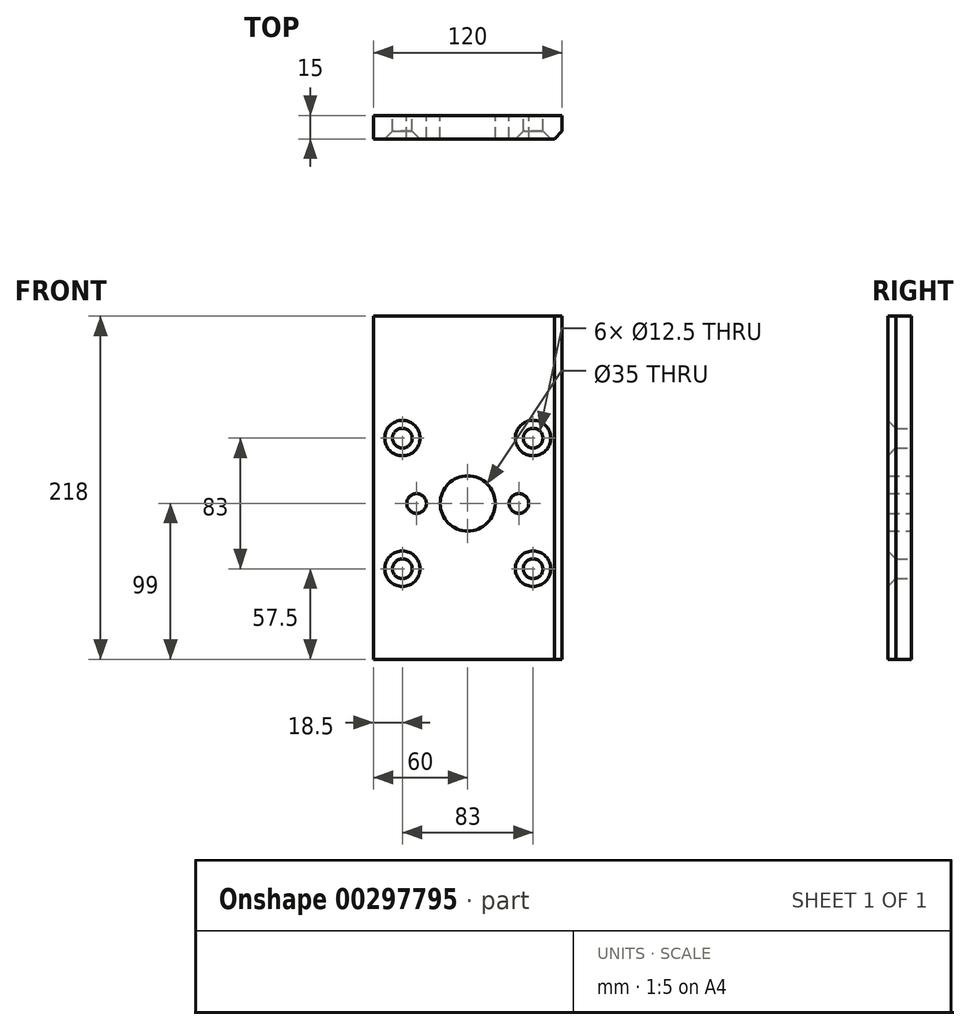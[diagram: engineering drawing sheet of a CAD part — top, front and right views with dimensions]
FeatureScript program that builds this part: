
annotation { "Feature Type Name" : "Feature", "Feature Type Description" : "" }
export const myFeature = defineFeature(function(context is Context, id is Id, definition is map)
    precondition{}
    {
        {
            var Q0;
            Q0=qCreatedBy(makeId("Front.planeOp"),FACE);
            var sketch = newSketch(context, id + "F0", { "sketchPlane" : qUnion([Q0])});
            skLineSegment(sketch, "E0.bottom", {"start": v(60, 119) * mm, "end": v(-60, 119) * mm});
            skLineSegment(sketch, "E0.top", {"start": v(60, -99) * mm, "end": v(-60, -99) * mm});
            skLineSegment(sketch, "E0.left", {"start": v(60, 119) * mm, "end": v(60, -99) * mm});
            skLineSegment(sketch, "E0.right", {"start": v(-60, 119) * mm, "end": v(-60, -99) * mm});
            skPoint(sketch, "E0.middle", {"position": v(0, 0) * mm});
            skCircle(sketch, "E1", {"center": v(0, 0) * mm, "radius": 17.5 * mm});
            skCircle(sketch, "E2", {"center": v(0, 0) * mm, "radius": 32.5 * mm, "construction": true});
            skCircle(sketch, "E3", {"center": v(-32.5, 0) * mm, "radius": 6.25 * mm});
            skCircle(sketch, "E4", {"center": v(32.5, 0) * mm, "radius": 6.25 * mm});
            skLineSegment(sketch, "E5.bottom", {"start": v(41.5, 41.5) * mm, "end": v(-41.5, 41.5) * mm, "construction": true});
            skLineSegment(sketch, "E5.top", {"start": v(41.5, -41.5) * mm, "end": v(-41.5, -41.5) * mm, "construction": true});
            skLineSegment(sketch, "E5.left", {"start": v(41.5, 41.5) * mm, "end": v(41.5, -41.5) * mm, "construction": true});
            skLineSegment(sketch, "E5.right", {"start": v(-41.5, 41.5) * mm, "end": v(-41.5, -41.5) * mm, "construction": true});
            skCircle(sketch, "E6", {"center": v(-41.5, 41.5) * mm, "radius": 6.25 * mm});
            skCircle(sketch, "E7", {"center": v(41.5, 41.5) * mm, "radius": 6.25 * mm});
            skCircle(sketch, "E8", {"center": v(41.5, -41.5) * mm, "radius": 6.25 * mm});
            skCircle(sketch, "E9", {"center": v(-41.5, -41.5) * mm, "radius": 6.25 * mm});
            skLineSegment(sketch, "E10", {"start": v(-60, 0) * mm, "end": v(60, 0) * mm, "construction": true});
            skSolve(sketch);
        }
        {
            var Q0;
            Q0=qSketchRegion(id+"F0",true);
            extrude(context, id + "F1", {"entities" : qUnion([Q0]), "depth" : 15 * mm});
        }
        {
            var Q0;
            Q0=makeQuery(id+"F1.opExtrude","CAP_EDGE",EDGE,{"disambiguationData":[OSD([sQuery(id+"F0.wireOp",EDGE,"E6")])],"isStart":false});
            var Q1;
            Q1=makeQuery(id+"F1.opExtrude","CAP_EDGE",EDGE,{"disambiguationData":[OSD([sQuery(id+"F0.wireOp",EDGE,"E7")])],"isStart":false});
            var Q2;
            Q2=makeQuery(id+"F1.opExtrude","CAP_EDGE",EDGE,{"disambiguationData":[OSD([sQuery(id+"F0.wireOp",EDGE,"E9")])],"isStart":false});
            var Q3;
            Q3=makeQuery(id+"F1.opExtrude","CAP_EDGE",EDGE,{"disambiguationData":[OSD([sQuery(id+"F0.wireOp",EDGE,"E8")])],"isStart":false});
            var Q4;
            Q4=makeQuery(id+"F1.opExtrude","CAP_EDGE",EDGE,{"disambiguationData":[OSD([sQuery(id+"F0.wireOp",EDGE,"E0.left")])],"isStart":false});
            chamfer(context, id + "F2", {"entities" : qUnion([Q0, Q1, Q2, Q3, Q4]), "chamferType" : ChamferType.OFFSET_ANGLE, "width" : 5 * mm, "oppositeDirection" : false, "angle" : 45 * degree, "tangentPropagation" : true});
        }
    });
